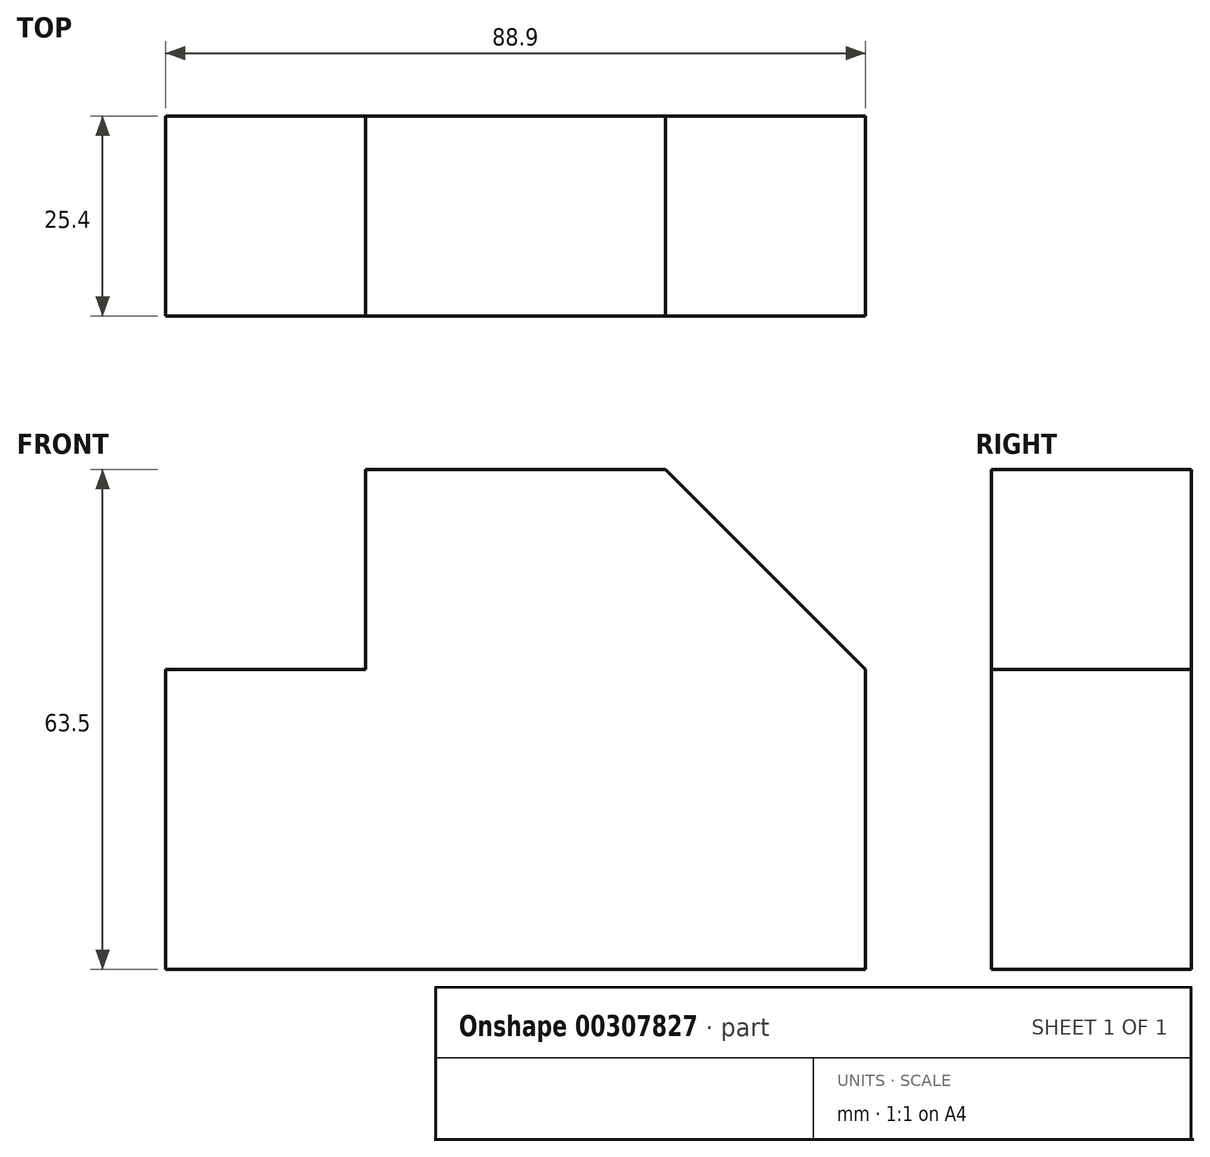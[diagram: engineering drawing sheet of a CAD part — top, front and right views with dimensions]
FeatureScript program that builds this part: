
annotation { "Feature Type Name" : "Feature", "Feature Type Description" : "" }
export const myFeature = defineFeature(function(context is Context, id is Id, definition is map)
    precondition{}
    {
        {
            var Q0;
            Q0=qCreatedBy(makeId("Front.planeOp"),FACE);
            var sketch = newSketch(context, id + "F0", { "sketchPlane" : qUnion([Q0])});
            skLineSegment(sketch, "E0", {"start": v(-34.72, -34.46) * mm, "end": v(54.18, -34.46) * mm});
            skLineSegment(sketch, "E1", {"start": v(-34.72, -34.46) * mm, "end": v(-34.72, 3.64) * mm});
            skLineSegment(sketch, "E2", {"start": v(-34.72, 3.64) * mm, "end": v(-9.32, 3.64) * mm});
            skLineSegment(sketch, "E3", {"start": v(-9.32, 3.64) * mm, "end": v(-9.32, 29.04) * mm});
            skLineSegment(sketch, "E4", {"start": v(-9.32, 29.04) * mm, "end": v(28.78, 29.04) * mm});
            skLineSegment(sketch, "E5", {"start": v(54.18, -34.46) * mm, "end": v(54.18, 3.64) * mm});
            skLineSegment(sketch, "E6", {"start": v(54.18, 3.64) * mm, "end": v(28.78, 29.04) * mm});
            skSolve(sketch);
        }
        {
            var Q0;
            Q0=makeQuery(id+"F0.imprint","IMPRINT",FACE,{"disambiguationData":[TD([[makeQuery(id+"F0.imprint","IMPRINT",EDGE,{"derivedFrom":sQuery(id+"F0.wireOp",EDGE,"E0")}),1.0]])]});
            extrude(context, id + "F1", {"entities" : qUnion([Q0]), "depth" : 25.4 * mm});
        }
    });
